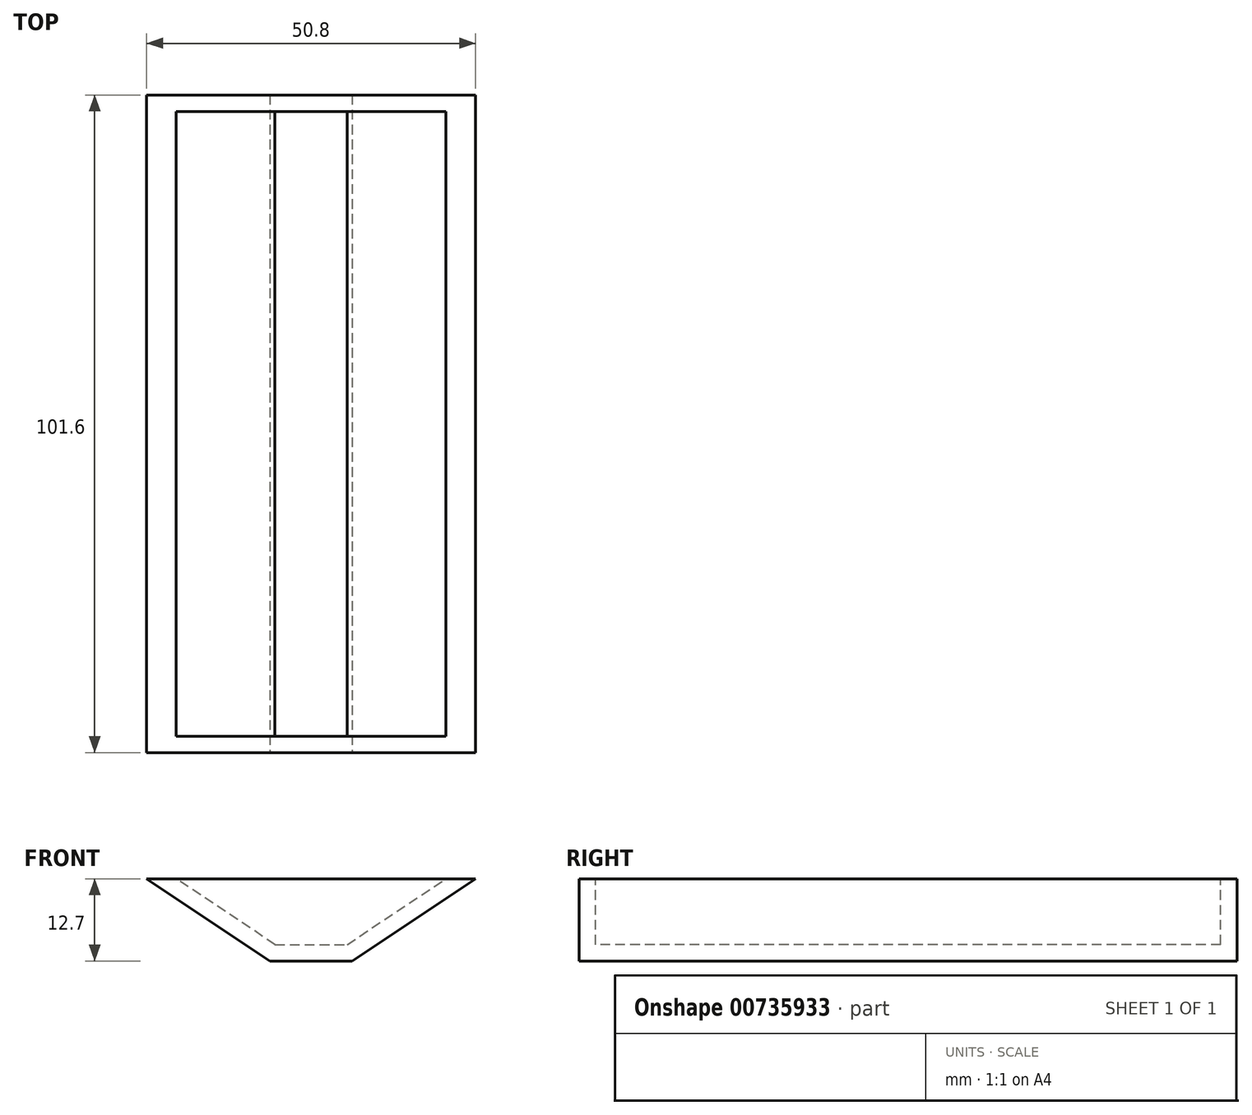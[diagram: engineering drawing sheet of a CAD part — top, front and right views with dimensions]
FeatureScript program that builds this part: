
annotation { "Feature Type Name" : "Feature", "Feature Type Description" : "" }
export const myFeature = defineFeature(function(context is Context, id is Id, definition is map)
    precondition{}
    {
        {
            var Q0;
            Q0=qCreatedBy(makeId("Front.planeOp"),FACE);
            var sketch = newSketch(context, id + "F0", { "sketchPlane" : qUnion([Q0])});
            skLineSegment(sketch, "E0", {"start": v(0, 0) * mm, "end": v(50.8, 0) * mm});
            skLineSegment(sketch, "E1", {"start": v(50.8, 0) * mm, "end": v(50.8, 12.7) * mm});
            skLineSegment(sketch, "E2", {"start": v(50.8, 12.7) * mm, "end": v(0, 12.7) * mm});
            skLineSegment(sketch, "E3", {"start": v(0, 12.7) * mm, "end": v(0, 0) * mm});
            skSolve(sketch);
        }
        {
            var Q0;
            Q0=makeQuery(id+"F0.imprint","IMPRINT",FACE,{"disambiguationData":[TD([[makeQuery(id+"F0.imprint","IMPRINT",EDGE,{"derivedFrom":sQuery(id+"F0.wireOp",EDGE,"E0")}),1.0]])]});
            extrude(context, id + "F1", {"entities" : qUnion([Q0]), "oppositeDirection" : true, "depth" : 101.6 * mm, "offsetDistance" : 25.4 * mm});
        }
        {
            var Q0;
            Q0=makeQuery(id+"F1.opExtrude","CAP_FACE",FACE,{"disambiguationData":[OSD([sQuery(id+"F0.wireOp",EDGE,"E0"),sQuery(id+"F0.wireOp",EDGE,"E1"),sQuery(id+"F0.wireOp",EDGE,"E2"),sQuery(id+"F0.wireOp",EDGE,"E3")])],"isStart":true});
            var sketch = newSketch(context, id + "F2", { "sketchPlane" : qUnion([Q0])});
            skLineSegment(sketch, "E4", {"start": v(0, 0) * mm, "end": v(19.05, 0) * mm});
            skLineSegment(sketch, "E5", {"start": v(19.05, 0) * mm, "end": v(0, 12.7) * mm});
            skLineSegment(sketch, "E6", {"start": v(0, 12.7) * mm, "end": v(0, 0) * mm});
            skSolve(sketch);
        }
        {
            var Q0;
            Q0=makeQuery(id+"F2.imprint","IMPRINT",FACE,{"disambiguationData":[TD([[makeQuery(id+"F2.imprint","IMPRINT",EDGE,{"derivedFrom":sQuery(id+"F2.wireOp",EDGE,"E4")}),1.0]])]});
            extrude(context, id + "F3", {"entities" : qUnion([Q0]), "operationType" : NewBodyOperationType.REMOVE, "oppositeDirection" : true, "depth" : 101.6 * mm, "offsetDistance" : 25.4 * mm});
        }
        {
            var Q0;
            Q0=makeQuery(id+"F1.opExtrude","CAP_FACE",FACE,{"disambiguationData":[OSD([sQuery(id+"F0.wireOp",EDGE,"E0"),sQuery(id+"F0.wireOp",EDGE,"E1"),sQuery(id+"F0.wireOp",EDGE,"E2"),sQuery(id+"F0.wireOp",EDGE,"E3")])],"isStart":true});
            var sketch = newSketch(context, id + "F4", { "sketchPlane" : qUnion([Q0])});
            skLineSegment(sketch, "E7", {"start": v(50.8, 0) * mm, "end": v(31.75, 0) * mm});
            skLineSegment(sketch, "E8", {"start": v(31.75, 0) * mm, "end": v(50.8, 12.7) * mm});
            skLineSegment(sketch, "E9", {"start": v(50.8, 12.7) * mm, "end": v(50.8, 0) * mm});
            skSolve(sketch);
        }
        {
            var Q0;
            Q0=makeQuery(id+"F4.imprint","IMPRINT",FACE,{"disambiguationData":[TD([[makeQuery(id+"F4.imprint","IMPRINT",EDGE,{"derivedFrom":sQuery(id+"F4.wireOp",EDGE,"E7")}),1.0]])]});
            extrude(context, id + "F5", {"entities" : qUnion([Q0]), "operationType" : NewBodyOperationType.REMOVE, "oppositeDirection" : true, "depth" : 101.6 * mm, "offsetDistance" : 25.4 * mm});
        }
        {
            var Q0;
            Q0=makeQuery(id+"F1.opExtrude","SWEPT_FACE",FACE,{"disambiguationData":[OSD([sQuery(id+"F0.wireOp",EDGE,"E2")])]});
            shell(context, id + "F6", {"entities" : qUnion([Q0]), "thickness" : 2.54 * mm});
        }
    });
